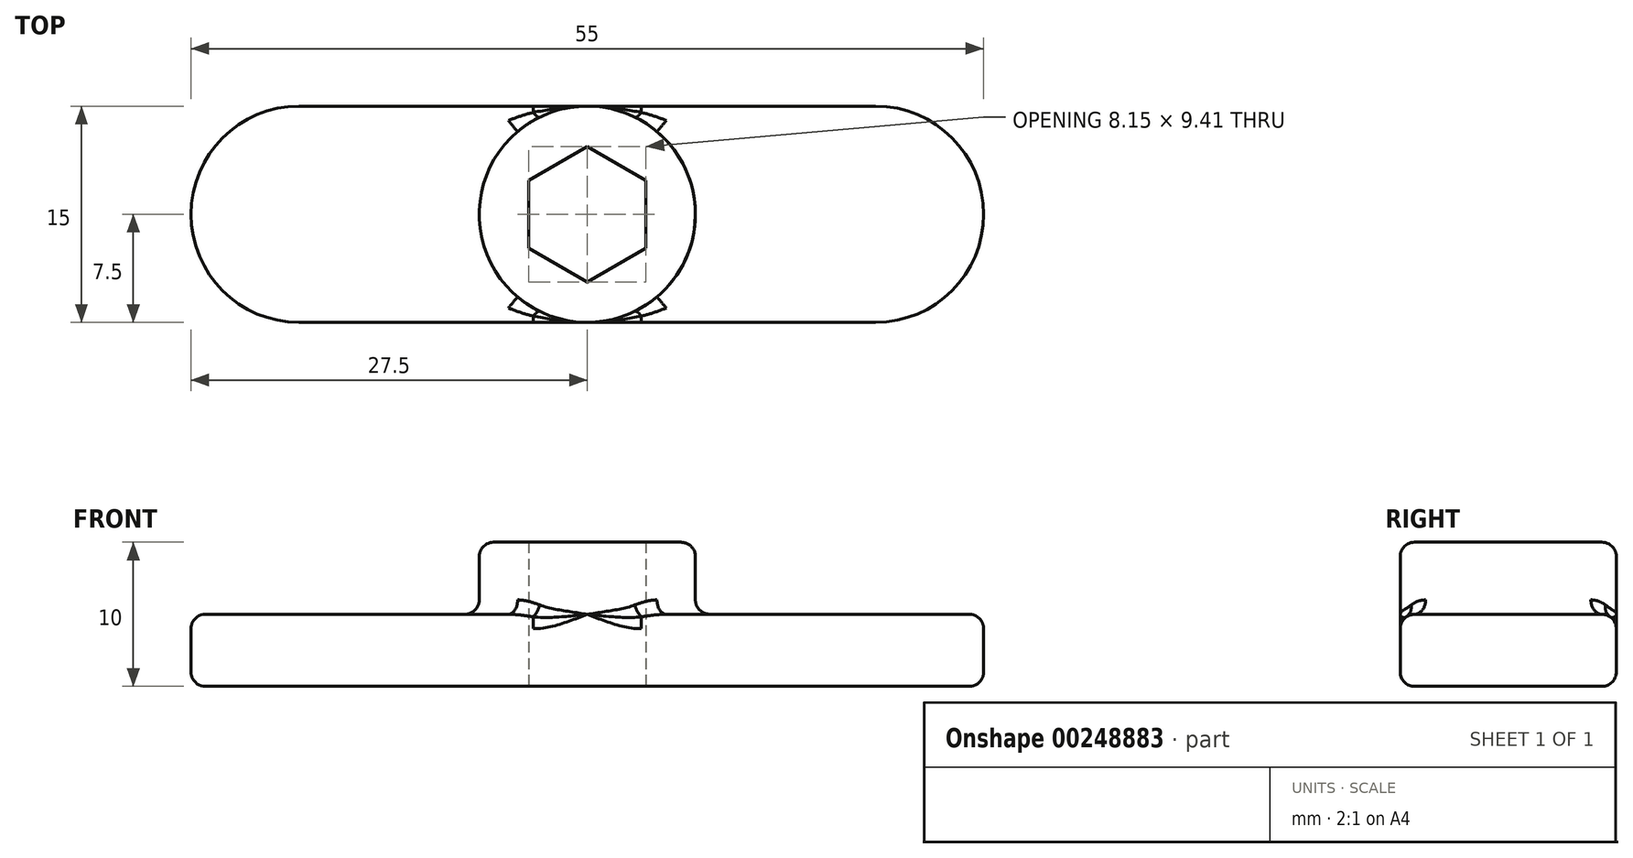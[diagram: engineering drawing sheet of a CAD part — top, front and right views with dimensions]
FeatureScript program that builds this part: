
annotation { "Feature Type Name" : "Feature", "Feature Type Description" : "" }
export const myFeature = defineFeature(function(context is Context, id is Id, definition is map)
    precondition{}
    {
        {
            var Q0;
            Q0=qCreatedBy(makeId("Top.planeOp"),FACE);
            var sketch = newSketch(context, id + "F0", { "sketchPlane" : qUnion([Q0])});
            skLineSegment(sketch, "E0", {"start": v(-20, 0) * mm, "end": v(20, 0) * mm, "construction": true});
            skArc(sketch, "E1.0.startCap", {"start": v(-20, -7.5) * mm, "mid": v(-27.5, 0) * mm, "end": v(-20, 7.5) * mm});
            skArc(sketch, "E1.0.endCap", {"start": v(20, 7.5) * mm, "mid": v(27.5, 0) * mm, "end": v(20, -7.5) * mm});
            skLineSegment(sketch, "E1.0.left", {"start": v(-20, 7.5) * mm, "end": v(20, 7.5) * mm});
            skLineSegment(sketch, "E1.0.right", {"start": v(-20, -7.5) * mm, "end": v(20, -7.5) * mm});
            skSolve(sketch);
        }
        {
            var Q0;
            Q0 = qSketchRegion(id + "F0", true);
            extrude(context, id + "F1", {"entities" : qUnion([Q0]), "depth" : 5 * mm});
        }
        {
            var Q0;
            Q0=makeQuery(id+"F1.opExtrude","CAP_FACE",FACE,{"disambiguationData":[OSD([sQuery(id+"F0.wireOp",EDGE,"E1.0.startCap"),sQuery(id+"F0.wireOp",EDGE,"E1.0.endCap"),sQuery(id+"F0.wireOp",EDGE,"E1.0.left"),sQuery(id+"F0.wireOp",EDGE,"E1.0.right")])],"isStart":false});
            var sketch = newSketch(context, id + "F2", { "sketchPlane" : qUnion([Q0])});
            skCircle(sketch, "E2", {"center": v(0, 0) * mm, "radius": 7.5 * mm});
            skSolve(sketch);
        }
        {
            var Q0;
            Q0 = qSketchRegion(id + "F2", true);
            extrude(context, id + "F3", {"entities" : qUnion([Q0]), "operationType" : NewBodyOperationType.ADD, "depth" : 5 * mm});
        }
        {
            var Q0;
            Q0=qCreatedBy(makeId("Top.planeOp"),FACE);
            var sketch = newSketch(context, id + "F4", { "sketchPlane" : qUnion([Q0])});
            skCircle(sketch, "E3.cCircle", {"center": v(0, 0) * mm, "radius": 4.08 * mm, "construction": true});
            skLineSegment(sketch, "E3.0", {"start": v(4.08, 2.35) * mm, "end": v(4.08, -2.35) * mm});
            skLineSegment(sketch, "E3.1", {"start": v(4.08, -2.35) * mm, "end": v(0, -4.7) * mm});
            skLineSegment(sketch, "E3.2", {"start": v(0, -4.7) * mm, "end": v(-4.08, -2.35) * mm});
            skLineSegment(sketch, "E3.3", {"start": v(-4.07, -2.35) * mm, "end": v(-4.08, 2.35) * mm});
            skLineSegment(sketch, "E3.4", {"start": v(-4.08, 2.35) * mm, "end": v(0, 4.7) * mm});
            skLineSegment(sketch, "E3.5", {"start": v(0, 4.7) * mm, "end": v(4.08, 2.35) * mm});
            skPoint(sketch, "E3.0.midPoint", {"position": v(4.08, 0) * mm});
            skSolve(sketch);
        }
        {
            var Q0;
            Q0 = qSketchRegion(id + "F4", true);
            extrude(context, id + "F5", {"entities" : qUnion([Q0]), "operationType" : NewBodyOperationType.REMOVE, "endBound" : BoundingType.THROUGH_ALL, "depth" : 25 * mm});
        }
        {
            var Q0;
            Q0=makeQuery(id+"F1.opExtrude","CAP_EDGE",EDGE,{"disambiguationData":[OSD([sQuery(id+"F0.wireOp",EDGE,"E1.0.startCap")])],"isStart":false});
            var Q1;
            Q1=makeQuery(id+"F1.opExtrude","CAP_EDGE",EDGE,{"disambiguationData":[OSD([sQuery(id+"F0.wireOp",EDGE,"E1.0.startCap")])],"isStart":true});
            var Q2;
            Q2=makeQuery(id+"F3.opExtrude","CAP_EDGE",EDGE,{"disambiguationData":[OSD([sQuery(id+"F2.wireOp",EDGE,"E2")])],"isStart":false});
            fillet(context, id + "F6", {"entities" : qUnion([Q0, Q1, Q2]), "radius" : 1 * mm, "tangentPropagation" : true, "allowEdgeOverflow" : false});
        }
        {
            var Q0;
            Q0=makeQuery(id+"F3.boolean.opBoolean","SPLIT",EDGE,{"disambiguationData":[OD(0.0)],"derivedFrom":makeQuery(id+"F3.opExtrude","CAP_EDGE",EDGE,{"disambiguationData":[OSD([sQuery(id+"F2.wireOp",EDGE,"E2")])],"isStart":true})});
            var Q1;
            Q1=makeQuery(id+"F3.boolean.opBoolean","SPLIT",EDGE,{"disambiguationData":[OD(1.0)],"derivedFrom":makeQuery(id+"F3.opExtrude","CAP_EDGE",EDGE,{"disambiguationData":[OSD([sQuery(id+"F2.wireOp",EDGE,"E2")])],"isStart":true})});
            fillet(context, id + "F7", {"entities" : qUnion([Q0, Q1]), "radius" : 1 * mm, "tangentPropagation" : true, "allowEdgeOverflow" : false});
        }
    });
